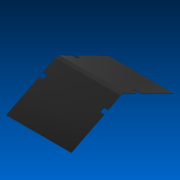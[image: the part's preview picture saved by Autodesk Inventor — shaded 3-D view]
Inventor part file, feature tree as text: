
AUTODESK INVENTOR PART (.ipt)
format: ipt  version: 2022.2 (Build 262287000, 287)  size: 153,600 bytes
history: native  units: in
note: dims shown in document units (in); Inventor stores cm internally (conversion verified against a paired STEP export)
features: sketch x4, extrude x3, hole x1
ambient origin geometry x8: Origin, YZ Plane, XZ Plane, XY Plane, X Axis, Y Axis, Z Axis, Center Point
bodies: Solid1 (feature_tree)
feature tree (8):
  extrude  "Extrusion1"  Depth=1.0in
  hole  "Hole1"  [1 undecoded]
  extrude  "Extrusion2"  Depth=1.0in
  extrude  "Extrusion3"  Depth=1.0in
  sketch  "Sketch1"  dims[d0=16.0in d1=1.0in]
  sketch  "Sketch2"  dims[d2=0.0625in d3=0.0in d4=1.0in]
  sketch  "Sketch3"  dims[d5=1.0in d6=1.0in]
  sketch  "Sketch4"  dims[d7=1.0in d8=1.0in d9=1.0in d10=3.0in d11=3.0in d12=0.17in d13=0.75in d14=0.375in d15=0.25in d16=0.5635in d17=1.0in d18=0.8108in d19=1.0in d20=4.09in d21=8.1531in d22=7.14in d23=1.0in d24=0.0625in d25=0.0in d26=1.0in d27=0.0in d28=0.0in d29=4.0in]
note: 1 required parameter value undecoded (feature->parameter linkage not recoverable at this tier; creation-order binding heuristic only, values carry confidence <= 0.55)
